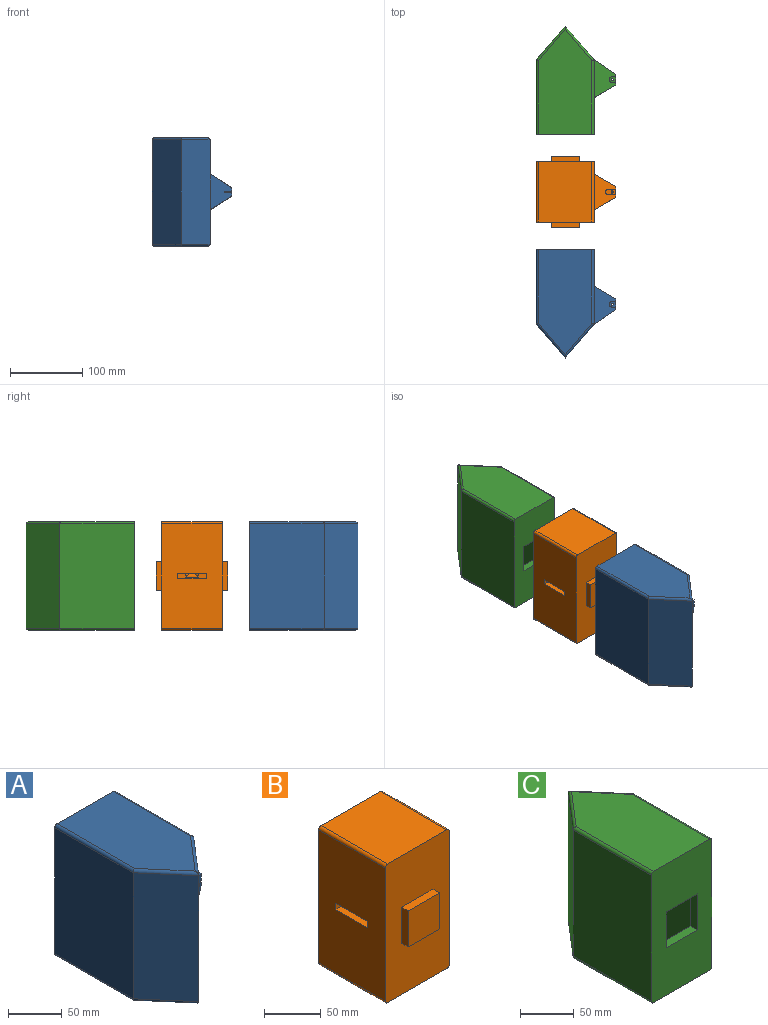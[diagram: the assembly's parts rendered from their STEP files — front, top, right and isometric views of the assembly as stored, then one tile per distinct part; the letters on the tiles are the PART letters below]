
ASSEMBLY  parts=3 mates=2
PART A: 59 faces, bbox 110x150x150 mm
  f0: cylinder r=1.5mm len=5mm, axis (0,0,1), area 47.1mm2, adj f18,f29
  f1: plane 52.32x30mm, normal (0.51,0,-0.86), area 1101.7mm2, adj f2,f3,f4,f7,f26,f27,f28
  f2: plane 15x5mm, normal (1,0,0), area 75mm2, adj f1,f3,f4,f18,f29
  f3: plane 49x30mm, normal (0.55,-0.83,0), area 1075.7mm2, adj f1,f2,f11,f16,f17,f18,f19,f20
  f4: plane 49x30mm, normal (0.5,0.87,0), area 1033.5mm2, adj f1,f2,f7,f16,f17,f18,f19,f20
  f5: plane 150x80mm, normal (0,1,0), area 10311.3mm2, adj f6,f7,f8,f9,f12,f13,f14,f15
  f6: plane 145.39x74mm, normal (0,0,-1), area 9161.7mm2, adj f5,f30,f31,f32,f33
  f7: plane 144x103.33mm, normal (1,0,0), area 12316.3mm2, adj f1,f4,f5,f11,f16,f33,f37
  f8: plane 145.39x74mm, normal (0,0,1), area 9161.7mm2, adj f5,f34,f35,f36,f37
  f9: plane 144x103.33mm, normal (-1,0,0), area 14880mm2, adj f5,f10,f30,f34
  f10: plane 144x46.67mm, normal (-0.76,-0.65,0), area 8850.8mm2, adj f9,f11,f31,f35
  f11: plane 144x46.67mm, normal (0.76,-0.65,0), area 8850.8mm2, adj f3,f7,f10,f32,f36
  f12: plane 41x9mm, normal (1,0,0), area 369mm2, adj f5,f13,f15,f52
  f13: plane 41x9mm, normal (0,0,1), area 369mm2, adj f5,f12,f14,f52
  f14: plane 41x9mm, normal (-1,0,0), area 369mm2, adj f5,f13,f15,f52
  f15: plane 41x9mm, normal (0,0,-1), area 369mm2, adj f5,f12,f14,f52
  f16: plane 52.32x30mm, normal (0.54,0,0.84), area 1118.2mm2, adj f3,f4,f7,f17,f22,f23,f24
  f17: plane 15x5mm, normal (1,0,0), area 75mm2, adj f3,f4,f16,f19,f25
  f18: plane 27.44x10mm, normal (0,0,1), area 205.1mm2, adj f0,f2,f3,f4,f20
  f19: plane 27.44x10mm, normal (0,0,-1), area 205.1mm2, adj f3,f4,f17,f20,f21
  f20: plane 27.44x2mm, normal (1,0,0), area 54.9mm2, adj f3,f4,f18,f19
  f21: cylinder r=1.5mm len=5mm, axis (0,0,1), area 47.1mm2, adj f19,f25
  f22: cylinder r=4mm len=8mm, axis (0,0,-1), area 60.1mm2, adj f16,f23,f24,f25
  f23: plane 5x3.17mm, normal (0,1,0), area 7.9mm2, adj f16,f22,f25
  f24: plane 5x3.17mm, normal (0,-1,0), area 7.9mm2, adj f16,f22,f25
  f25: plane 9x8mm, normal (0,0,1), area 58.1mm2, adj f17,f21,f22,f23,f24
  f26: cylinder r=4mm len=8mm, axis (0,0,1), area 56.9mm2, adj f1,f27,f28,f29
  f27: plane 5x3mm, normal (0,1,0), area 7.5mm2, adj f1,f26,f29
  f28: plane 5x3mm, normal (0,-1,0), area 7.5mm2, adj f1,f26,f29
  f29: plane 9x8mm, normal (0,0,-1), area 58.1mm2, adj f0,f2,f26,f27,f28
  f30: cylinder r=3mm len=103.33mm, axis (0,-1,0), area 485mm2, adj f5,f6,f9,f31
  f31: cylinder r=3mm len=48.62mm, axis (-0.65,0.76,0), area 281.7mm2, adj f6,f10,f30,f32
  f32: cylinder r=3mm len=48.62mm, axis (0.65,0.76,0), area 281.7mm2, adj f6,f11,f31,f33
  f33: cylinder r=3mm len=103.33mm, axis (0,1,0), area 485mm2, adj f5,f6,f7,f32
  f34: cylinder r=3mm len=103.33mm, axis (0,1,0), area 485mm2, adj f5,f8,f9,f35
  f35: cylinder r=3mm len=48.62mm, axis (0.65,-0.76,0), area 281.7mm2, adj f8,f10,f34,f36
  f36: cylinder r=3mm len=48.62mm, axis (-0.65,-0.76,0), area 281.7mm2, adj f8,f11,f35,f37
  f37: cylinder r=3mm len=103.33mm, axis (0,-1,0), area 485mm2, adj f5,f7,f8,f36
  f38: plane 43.42x25.01mm, normal (-0.5,-0.87,0), area 739mm2, adj f39,f43,f53,f54,f55,f56,f57,f58
  f39: plane 47.58x25.28mm, normal (-0.51,0,0.86), area 861.7mm2, adj f38,f40,f43,f47,f54,f58
  f40: plane 41.38x23.87mm, normal (-0.55,0.83,0), area 685.2mm2, adj f39,f47,f53,f54,f55,f56,f57
  f41: plane 140x70mm, normal (0,-1,0), area 7199mm2, adj f42,f43,f44,f45,f48,f49,f50,f51
  f42: plane 137.32x70mm, normal (0,0,1), area 8183mm2, adj f41,f43,f45,f46,f47
  f43: plane 140x96.48mm, normal (-1,0,0), area 11441.7mm2, adj f38,f39,f41,f42,f44,f47,f53
  f44: plane 137.32x70mm, normal (0,0,-1), area 8183mm2, adj f41,f43,f45,f46,f47
  f45: plane 140x96.48mm, normal (1,0,0), area 13507.7mm2, adj f41,f42,f44,f46
  f46: plane 140x40.83mm, normal (0.76,0.65,0), area 7529.3mm2, adj f42,f44,f45,f47
  f47: plane 140x42.76mm, normal (-0.76,0.65,0), area 7637mm2, adj f39,f40,f42,f43,f44,f46,f53
  f48: plane 51x4mm, normal (-1,0,0), area 204mm2, adj f41,f49,f51,f52
  f49: plane 51x4mm, normal (0,0,-1), area 204mm2, adj f41,f48,f50,f52
  f50: plane 51x4mm, normal (1,0,0), area 204mm2, adj f41,f49,f51,f52
  f51: plane 51x4mm, normal (0,0,1), area 204mm2, adj f41,f48,f50,f52
  f52: plane 51x51mm, normal (0,-1,0), area 920mm2, adj f12,f13,f14,f15,f48,f49,f50,f51
  f53: plane 47.58x25.52mm, normal (-0.54,0,-0.84), area 874.7mm2, adj f38,f40,f43,f47,f57
  f54: plane 21.88x5.28mm, normal (0,0,-1), area 51.9mm2, adj f38,f39,f40,f56,f58
  f55: plane 21.88x5.52mm, normal (0,0,1), area 51.9mm2, adj f38,f40,f56,f57
  f56: plane 21.88x12mm, normal (-1,0,0), area 262.5mm2, adj f38,f40,f54,f55
  f57: cylinder r=9mm len=15.3mm, axis (0,0,-1), area 36.8mm2, adj f38,f40,f53,f55
  f58: cylinder r=9mm len=15.16mm, axis (0,0,1), area 30.8mm2, adj f38,f39,f54
PART B: 53 faces, bbox 110x99.3x150 mm
  f0: plane 49.64x30mm, normal (0.54,0,0.84), area 1026mm2, adj f3,f4,f5,f21,f31,f32,f34
  f1: plane 49.64x30mm, normal (0.54,0,-0.84), area 1070.6mm2, adj f2,f3,f4,f5,f28,f29,f30
  f2: plane 15x5mm, normal (1,0,0), area 75mm2, adj f1,f3,f4,f22,f27
  f3: plane 50x30mm, normal (0.5,0.87,0), area 1050.8mm2, adj f0,f1,f2,f5,f21,f22,f23,f24
  f4: plane 50x30mm, normal (0.5,-0.87,0), area 1050.8mm2, adj f0,f1,f2,f5,f21,f22,f23,f24
  f5: plane 144x83.33mm, normal (1,0,0), area 9517.9mm2, adj f0,f1,f3,f4,f6,f10,f49,f50
  f6: plane 150x80mm, normal (0,-1,0), area 10471.3mm2, adj f5,f7,f8,f9,f11,f12,f13,f14
  f7: plane 83.33x74mm, normal (0,0,-1), area 6166.7mm2, adj f6,f10,f49,f52
  f8: plane 83.33x74mm, normal (0,0,1), area 6166.7mm2, adj f6,f10,f50,f51
  f9: plane 144x83.33mm, normal (-1,0,0), area 11720mm2, adj f6,f10,f35,f36,f37,f38,f51,f52
  f10: plane 150x80mm, normal (0,1,0), area 10471.3mm2, adj f5,f7,f8,f9,f16,f17,f18,f19
  f11: plane 39x8mm, normal (0,0,-1), area 312mm2, adj f6,f12,f14,f15
  f12: plane 39x8mm, normal (1,0,0), area 312mm2, adj f6,f11,f13,f15
  f13: plane 39x8mm, normal (0,0,1), area 312mm2, adj f6,f12,f14,f15
  f14: plane 39x8mm, normal (-1,0,0), area 312mm2, adj f6,f11,f13,f15
  f15: plane 39x39mm, normal (0,-1,0), area 1521mm2, adj f11,f12,f13,f14
  f16: plane 39x8mm, normal (0,0,-1), area 312mm2, adj f10,f17,f19,f20
  f17: plane 39x8mm, normal (-1,0,0), area 312mm2, adj f10,f16,f18,f20
  f18: plane 39x8mm, normal (0,0,1), area 312mm2, adj f10,f17,f19,f20
  f19: plane 39x8mm, normal (1,0,0), area 312mm2, adj f10,f16,f18,f20
  f20: plane 39x39mm, normal (0,1,0), area 1521mm2, adj f16,f17,f18,f19
  f21: plane 15x5mm, normal (1,0,0), area 75mm2, adj f0,f3,f4,f23,f33
  f22: plane 26.55x10mm, normal (0,0,1), area 200.7mm2, adj f2,f3,f4,f24,f26
  f23: plane 26.55x10mm, normal (0,0,-1), area 200.7mm2, adj f3,f4,f21,f24,f25
  f24: plane 26.55x2mm, normal (1,0,0), area 53.1mm2, adj f3,f4,f22,f23
  f25: cylinder r=1.5mm len=5mm, axis (0,0,1), area 47.1mm2, adj f23,f33
  f26: cylinder r=1.5mm len=5mm, axis (0,0,1), area 47.1mm2, adj f22,f27
  f27: plane 9x8mm, normal (0,0,-1), area 58.1mm2, adj f2,f26,f28,f29,f30
  f28: plane 5x3.17mm, normal (0,1,0), area 7.9mm2, adj f1,f27,f30
  f29: plane 5x3.17mm, normal (0,-1,0), area 7.9mm2, adj f1,f27,f30
  f30: cylinder r=4mm len=8mm, axis (0,0,1), area 60.1mm2, adj f1,f27,f28,f29
  f31: plane 70x7.5mm, normal (0,1,0), area 295.9mm2, adj f0,f33,f34,f40,f41,f42,f44,f45
  f32: plane 70x7.5mm, normal (0,-1,0), area 295.9mm2, adj f0,f33,f34,f40,f41,f43,f44,f47
  f33: plane 25.67x8mm, normal (0,0,1), area 198.3mm2, adj f21,f25,f31,f32,f44
  f34: cylinder r=4mm len=62.11mm, axis (-1,0,0), area 729.9mm2, adj f0,f31,f32,f41
  f35: plane 62.5x7mm, normal (0,1,0), area 437.5mm2, adj f9,f36,f38,f39
  f36: plane 62.5x40mm, normal (0,0,-1), area 2005mm2, adj f9,f35,f37,f39,f42,f43,f48
  f37: plane 62.5x7mm, normal (0,-1,0), area 437.5mm2, adj f9,f36,f38,f39
  f38: plane 62.5x40mm, normal (0,0,1), area 2500mm2, adj f9,f35,f37,f39
  f39: plane 40x7mm, normal (-1,0,0), area 190mm2, adj f35,f36,f37,f38,f45,f46,f47
  f40: plane 12.5x8mm, normal (0,0,1), area 100mm2, adj f31,f32,f44,f46
  f41: plane 8x6.5mm, normal (1,0,0), area 45.1mm2, adj f31,f32,f34,f48
  f42: cylinder r=5mm len=32.5mm, axis (1,0,0), area 205.3mm2, adj f31,f36,f45,f48
  f43: cylinder r=5mm len=32.5mm, axis (-1,0,0), area 205.3mm2, adj f32,f36,f47,f48
  f44: cylinder r=5mm len=8mm, axis (0,-1,0), area 41.9mm2, adj f31,f32,f33,f40
  f45: cylinder r=5mm len=10mm, axis (0,0,-1), area 28.5mm2, adj f31,f39,f42,f46
  f46: cylinder r=5mm len=18mm, axis (0,1,0), area 91.4mm2, adj f39,f40,f45,f47
  f47: cylinder r=5mm len=10mm, axis (0,0,-1), area 28.5mm2, adj f32,f39,f43,f46
  f48: cylinder r=5mm len=18mm, axis (0,1,0), area 91.4mm2, adj f36,f41,f42,f43
  f49: cylinder r=3mm len=83.33mm, axis (0,-1,0), area 392.7mm2, adj f5,f6,f7,f10
  f50: cylinder r=3mm len=83.33mm, axis (0,1,0), area 392.7mm2, adj f5,f6,f8,f10
  f51: cylinder r=3mm len=83.33mm, axis (0,-1,0), area 392.7mm2, adj f6,f8,f9,f10
  f52: cylinder r=3mm len=83.33mm, axis (0,1,0), area 392.7mm2, adj f6,f7,f9,f10
PART C: 59 faces, bbox 110x150x150 mm
  f0: cylinder r=1.5mm len=5mm, axis (0,0,1), area 47.1mm2, adj f18,f29
  f1: plane 52.32x30mm, normal (0.51,0,-0.86), area 1101.7mm2, adj f2,f3,f4,f7,f26,f27,f28
  f2: plane 15x5mm, normal (1,0,0), area 75mm2, adj f1,f3,f4,f18,f29
  f3: plane 49x30mm, normal (0.55,0.83,0), area 1075.7mm2, adj f1,f2,f11,f16,f17,f18,f19,f20
  f4: plane 49x30mm, normal (0.5,-0.87,0), area 1033.5mm2, adj f1,f2,f7,f16,f17,f18,f19,f20
  f5: plane 150x80mm, normal (0,-1,0), area 10311.3mm2, adj f6,f7,f8,f9,f12,f13,f14,f15
  f6: plane 145.39x74mm, normal (0,0,-1), area 9161.7mm2, adj f5,f30,f31,f32,f33
  f7: plane 144x103.33mm, normal (1,0,0), area 12316.3mm2, adj f1,f4,f5,f11,f16,f33,f37
  f8: plane 145.39x74mm, normal (0,0,1), area 9161.7mm2, adj f5,f34,f35,f36,f37
  f9: plane 144x103.33mm, normal (-1,0,0), area 14880mm2, adj f5,f10,f30,f34
  f10: plane 144x46.67mm, normal (-0.76,0.65,0), area 8850.8mm2, adj f9,f11,f31,f35
  f11: plane 144x46.67mm, normal (0.76,0.65,0), area 8850.8mm2, adj f3,f7,f10,f32,f36
  f12: plane 41x9mm, normal (1,0,0), area 369mm2, adj f5,f13,f15,f52
  f13: plane 41x9mm, normal (0,0,1), area 369mm2, adj f5,f12,f14,f52
  f14: plane 41x9mm, normal (-1,0,0), area 369mm2, adj f5,f13,f15,f52
  f15: plane 41x9mm, normal (0,0,-1), area 369mm2, adj f5,f12,f14,f52
  f16: plane 52.32x30mm, normal (0.54,0,0.84), area 1118.2mm2, adj f3,f4,f7,f17,f22,f23,f24
  f17: plane 15x5mm, normal (1,0,0), area 75mm2, adj f3,f4,f16,f19,f25
  f18: plane 27.44x10mm, normal (0,0,1), area 205.1mm2, adj f0,f2,f3,f4,f20
  f19: plane 27.44x10mm, normal (0,0,-1), area 205.1mm2, adj f3,f4,f17,f20,f21
  f20: plane 27.44x2mm, normal (1,0,0), area 54.9mm2, adj f3,f4,f18,f19
  f21: cylinder r=1.5mm len=5mm, axis (0,0,1), area 47.1mm2, adj f19,f25
  f22: cylinder r=4mm len=8mm, axis (0,0,-1), area 60.1mm2, adj f16,f23,f24,f25
  f23: plane 5x3.17mm, normal (0,-1,0), area 7.9mm2, adj f16,f22,f25
  f24: plane 5x3.17mm, normal (0,1,0), area 7.9mm2, adj f16,f22,f25
  f25: plane 9x8mm, normal (0,0,1), area 58.1mm2, adj f17,f21,f22,f23,f24
  f26: cylinder r=4mm len=8mm, axis (0,0,1), area 56.9mm2, adj f1,f27,f28,f29
  f27: plane 5x3mm, normal (0,-1,0), area 7.5mm2, adj f1,f26,f29
  f28: plane 5x3mm, normal (0,1,0), area 7.5mm2, adj f1,f26,f29
  f29: plane 9x8mm, normal (0,0,-1), area 58.1mm2, adj f0,f2,f26,f27,f28
  f30: cylinder r=3mm len=103.33mm, axis (0,1,0), area 485mm2, adj f5,f6,f9,f31
  f31: cylinder r=3mm len=48.62mm, axis (-0.65,-0.76,0), area 281.7mm2, adj f6,f10,f30,f32
  f32: cylinder r=3mm len=48.62mm, axis (0.65,-0.76,0), area 281.7mm2, adj f6,f11,f31,f33
  f33: cylinder r=3mm len=103.33mm, axis (0,-1,0), area 485mm2, adj f5,f6,f7,f32
  f34: cylinder r=3mm len=103.33mm, axis (0,-1,0), area 485mm2, adj f5,f8,f9,f35
  f35: cylinder r=3mm len=48.62mm, axis (0.65,0.76,0), area 281.7mm2, adj f8,f10,f34,f36
  f36: cylinder r=3mm len=48.62mm, axis (-0.65,0.76,0), area 281.7mm2, adj f8,f11,f35,f37
  f37: cylinder r=3mm len=103.33mm, axis (0,1,0), area 485mm2, adj f5,f7,f8,f36
  f38: plane 43.42x25.01mm, normal (-0.5,0.87,0), area 739mm2, adj f39,f43,f53,f54,f55,f56,f57,f58
  f39: plane 47.58x25.28mm, normal (-0.51,0,0.86), area 861.7mm2, adj f38,f40,f43,f47,f54,f58
  f40: plane 41.38x23.87mm, normal (-0.55,-0.83,0), area 685.2mm2, adj f39,f47,f53,f54,f55,f56,f57
  f41: plane 140x70mm, normal (0,1,0), area 7199mm2, adj f42,f43,f44,f45,f48,f49,f50,f51
  f42: plane 137.32x70mm, normal (0,0,1), area 8183mm2, adj f41,f43,f45,f46,f47
  f43: plane 140x96.48mm, normal (-1,0,0), area 11441.7mm2, adj f38,f39,f41,f42,f44,f47,f53
  f44: plane 137.32x70mm, normal (0,0,-1), area 8183mm2, adj f41,f43,f45,f46,f47
  f45: plane 140x96.48mm, normal (1,0,0), area 13507.7mm2, adj f41,f42,f44,f46
  f46: plane 140x40.83mm, normal (0.76,-0.65,0), area 7529.3mm2, adj f42,f44,f45,f47
  f47: plane 140x42.76mm, normal (-0.76,-0.65,0), area 7637mm2, adj f39,f40,f42,f43,f44,f46,f53
  f48: plane 51x4mm, normal (-1,0,0), area 204mm2, adj f41,f49,f51,f52
  f49: plane 51x4mm, normal (0,0,-1), area 204mm2, adj f41,f48,f50,f52
  f50: plane 51x4mm, normal (1,0,0), area 204mm2, adj f41,f49,f51,f52
  f51: plane 51x4mm, normal (0,0,1), area 204mm2, adj f41,f48,f50,f52
  f52: plane 51x51mm, normal (0,1,0), area 920mm2, adj f12,f13,f14,f15,f48,f49,f50,f51
  f53: plane 47.58x25.52mm, normal (-0.54,0,-0.84), area 874.7mm2, adj f38,f40,f43,f47,f57
  f54: plane 21.88x5.28mm, normal (0,0,-1), area 51.9mm2, adj f38,f39,f40,f56,f58
  f55: plane 21.88x5.52mm, normal (0,0,1), area 51.9mm2, adj f38,f40,f56,f57
  f56: plane 21.88x12mm, normal (-1,0,0), area 262.5mm2, adj f38,f40,f54,f55
  f57: cylinder r=9mm len=15.3mm, axis (0,0,-1), area 36.8mm2, adj f38,f40,f53,f55
  f58: cylinder r=9mm len=15.16mm, axis (0,0,1), area 30.8mm2, adj f38,f39,f54
PLACE A t=(0.98,-71.42,-1.46)mm
PLACE B t=(0.98,-33.42,-1.46)mm fixed
PLACE C t=(0.98,4.58,-1.46)mm
MATE slider B.f20 <-> C.f5  axis (0,1,0) through (0.98,57.92,-1.46)mm
MATE slider B.f15 <-> A.f5  axis (0,-1,0) through (0.98,-41.42,-1.46)mm
